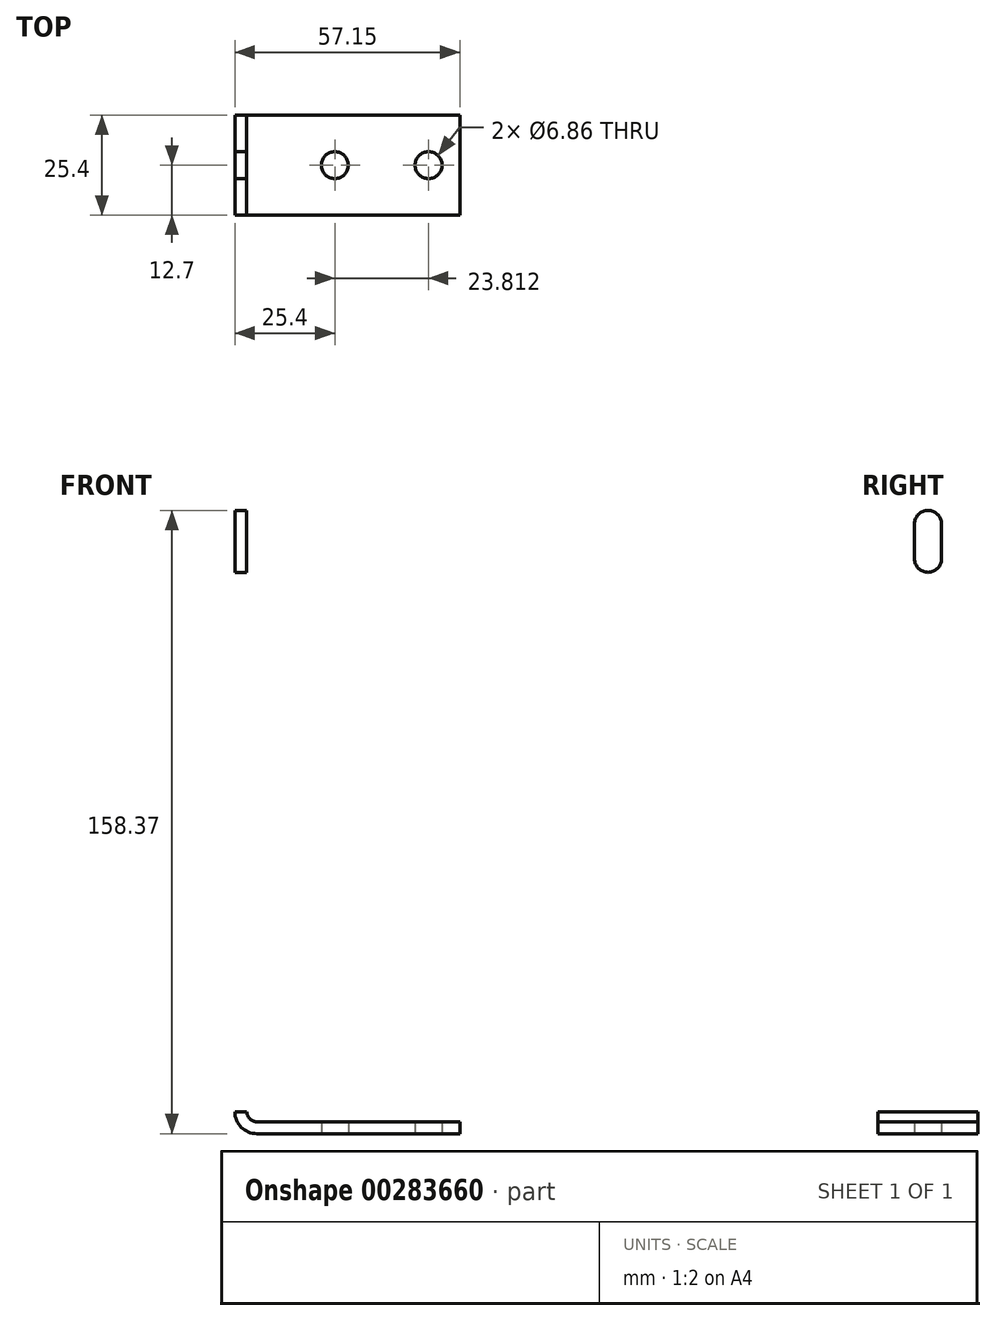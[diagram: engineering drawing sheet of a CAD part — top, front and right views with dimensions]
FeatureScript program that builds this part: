
annotation { "Feature Type Name" : "Feature", "Feature Type Description" : "" }
export const myFeature = defineFeature(function(context is Context, id is Id, definition is map)
    precondition{}
    {
        {
            var Q0;
            Q0=qCreatedBy(makeId("Front.planeOp"),FACE);
            var sketch = newSketch(context, id + "F0", { "sketchPlane" : qUnion([Q0])});
            skLineSegment(sketch, "E0", {"start": v(0, 171.45) * mm, "end": v(0, 5.58) * mm});
            skLineSegment(sketch, "E1", {"start": v(5.58, 0) * mm, "end": v(82.55, 0) * mm});
            skLineSegment(sketch, "E2", {"start": v(82.55, 0) * mm, "end": v(82.55, 3.04) * mm});
            skLineSegment(sketch, "E3", {"start": v(82.55, 3.04) * mm, "end": v(5.58, 3.04) * mm});
            skLineSegment(sketch, "E4", {"start": v(3.04, 5.58) * mm, "end": v(3.04, 171.45) * mm});
            skLineSegment(sketch, "E5", {"start": v(3.04, 171.45) * mm, "end": v(0, 171.45) * mm});
            skPoint(sketch, "E6.visualSharp", {"position": v(3.04, 3.04) * mm});
            skArc(sketch, "E6.filletArc", {"start": v(3.04, 5.58) * mm, "mid": v(3.78, 3.78) * mm, "end": v(5.58, 3.04) * mm});
            skPoint(sketch, "E7.visualSharp", {"position": v(0, 0) * mm});
            skArc(sketch, "E7.filletArc", {"start": v(0, 5.58) * mm, "mid": v(1.63, 1.63) * mm, "end": v(5.58, 0) * mm});
            skSolve(sketch);
        }
        {
            var Q0;
            Q0=makeQuery(id+"F0.imprint","IMPRINT",FACE,{"disambiguationData":[TD([[makeQuery(id+"F0.imprint","IMPRINT",EDGE,{"derivedFrom":sQuery(id+"F0.wireOp",EDGE,"E0")}),1.0]])]});
            extrude(context, id + "F1", {"entities" : qUnion([Q0]), "depth" : 25.4 * mm});
        }
        {
            var Q0;
            Q0=makeQuery(id+"F1.opExtrude","SWEPT_FACE",FACE,{"disambiguationData":[OSD([sQuery(id+"F0.wireOp",EDGE,"E0")])]});
            var sketch = newSketch(context, id + "F2", { "sketchPlane" : qUnion([Q0])});
            skLineSegment(sketch, "E8", {"start": v(12.7, 154.94) * mm, "end": v(12.7, 146.05) * mm, "construction": true});
            skPoint(sketch, "E8.startSnap0", {"position": v(12.7, 171.45) * mm});
            skArc(sketch, "E9.0.startCap", {"start": v(9.27, 154.94) * mm, "mid": v(12.7, 158.37) * mm, "end": v(16.13, 154.94) * mm});
            skArc(sketch, "E9.0.endCap", {"start": v(16.13, 146.05) * mm, "mid": v(12.7, 142.62) * mm, "end": v(9.27, 146.05) * mm});
            skLineSegment(sketch, "E9.0.left", {"start": v(16.13, 154.94) * mm, "end": v(16.13, 146.05) * mm});
            skLineSegment(sketch, "E9.0.right", {"start": v(9.27, 154.94) * mm, "end": v(9.27, 146.05) * mm});
            skCircle(sketch, "E10", {"center": v(12.7, 82.55) * mm, "radius": 3.43 * mm});
            skPoint(sketch, "E10.centerSnap0", {"position": v(12.7, 142.62) * mm});
            skCircle(sketch, "E11", {"center": v(12.7, 59.7) * mm, "radius": 3.43 * mm});
            skSolve(sketch);
        }
        {
            var Q0;
            Q0=makeQuery(id+"F2.imprint","IMPRINT",FACE,{"disambiguationData":[TD([[makeQuery(id+"F2.imprint","IMPRINT",EDGE,{"derivedFrom":sQuery(id+"F2.wireOp",EDGE,"E9.0.startCap")}),-1.0]])]});
            var Q1;
            Q1=makeQuery(id+"F2.imprint","IMPRINT",FACE,{"disambiguationData":[TD([[makeQuery(id+"F2.imprint","IMPRINT",EDGE,{"derivedFrom":sQuery(id+"F2.wireOp",EDGE,"E10")}),1.0]])]});
            var Q2;
            Q2=makeQuery(id+"F2.imprint","IMPRINT",FACE,{"disambiguationData":[TD([[makeQuery(id+"F2.imprint","IMPRINT",EDGE,{"derivedFrom":sQuery(id+"F2.wireOp",EDGE,"E11")}),1.0]])]});
            extrude(context, id + "F3", {"entities" : qUnion([Q0, Q1, Q2]), "operationType" : NewBodyOperationType.REMOVE, "endBound" : BoundingType.THROUGH_ALL, "oppositeDirection" : true, "depth" : 25.4 * mm});
        }
        {
            var Q0;
            Q0=makeQuery(id+"F1.opExtrude","SWEPT_FACE",FACE,{"disambiguationData":[OSD([sQuery(id+"F0.wireOp",EDGE,"E1")])]});
            var sketch = newSketch(context, id + "F4", { "sketchPlane" : qUnion([Q0])});
            skCircle(sketch, "E12", {"center": v(25.4, 12.7) * mm, "radius": 3.43 * mm});
            skPoint(sketch, "E12.centerSnap0", {"position": v(82.55, 12.7) * mm});
            skCircle(sketch, "E13", {"center": v(69.85, 12.7) * mm, "radius": 3.43 * mm});
            skSolve(sketch);
        }
        {
            var Q0;
            Q0=makeQuery(id+"F4.imprint","IMPRINT",FACE,{"disambiguationData":[TD([[makeQuery(id+"F4.imprint","IMPRINT",EDGE,{"derivedFrom":sQuery(id+"F4.wireOp",EDGE,"E12")}),1.0]])]});
            var Q1;
            Q1=makeQuery(id+"F4.imprint","IMPRINT",FACE,{"disambiguationData":[TD([[makeQuery(id+"F4.imprint","IMPRINT",EDGE,{"derivedFrom":sQuery(id+"F4.wireOp",EDGE,"E13")}),1.0]])]});
            extrude(context, id + "F5", {"entities" : qUnion([Q0, Q1]), "operationType" : NewBodyOperationType.REMOVE, "endBound" : BoundingType.THROUGH_ALL, "oppositeDirection" : true, "depth" : 25.4 * mm});
        }
        {
            var Q0;
            Q0=makeQuery(id+"F1.opExtrude","SWEPT_FACE",FACE,{"disambiguationData":[OSD([sQuery(id+"F0.wireOp",EDGE,"E1")])]});
            var sketch = newSketch(context, id + "F6", { "sketchPlane" : qUnion([Q0])});
            skLineSegment(sketch, "E14.bottom", {"start": v(82.55, 25.4) * mm, "end": v(57.15, 25.4) * mm});
            skLineSegment(sketch, "E14.top", {"start": v(82.55, 0) * mm, "end": v(57.15, 0) * mm});
            skLineSegment(sketch, "E14.left", {"start": v(82.55, 25.4) * mm, "end": v(82.55, 0) * mm});
            skLineSegment(sketch, "E14.right", {"start": v(57.15, 25.4) * mm, "end": v(57.15, 0) * mm});
            skSolve(sketch);
        }
        {
            var Q0;
            Q0=makeQuery(id+"F6.imprint","IMPRINT",FACE,{"disambiguationData":[TD([[makeQuery(id+"F6.imprint","IMPRINT",EDGE,{"derivedFrom":sQuery(id+"F6.wireOp",EDGE,"E14.bottom")}),-1.0]])]});
            extrude(context, id + "F7", {"entities" : qUnion([Q0]), "operationType" : NewBodyOperationType.REMOVE, "endBound" : BoundingType.THROUGH_ALL, "oppositeDirection" : true, "depth" : 25.4 * mm});
        }
        {
            var Q0;
            Q0=makeQuery(id+"F1.opExtrude","SWEPT_FACE",FACE,{"disambiguationData":[OSD([sQuery(id+"F0.wireOp",EDGE,"E1")])]});
            var sketch = newSketch(context, id + "F8", { "sketchPlane" : qUnion([Q0])});
            skCircle(sketch, "E15", {"center": v(49.21, 12.7) * mm, "radius": 3.43 * mm});
            skSolve(sketch);
        }
        {
            var Q0;
            Q0=makeQuery(id+"F8.imprint","IMPRINT",FACE,{"disambiguationData":[TD([[makeQuery(id+"F8.imprint","IMPRINT",EDGE,{"derivedFrom":sQuery(id+"F8.wireOp",EDGE,"E15")}),1.0]])]});
            extrude(context, id + "F9", {"entities" : qUnion([Q0]), "operationType" : NewBodyOperationType.REMOVE, "endBound" : BoundingType.THROUGH_ALL, "oppositeDirection" : true, "depth" : 25.4 * mm});
        }
    });
